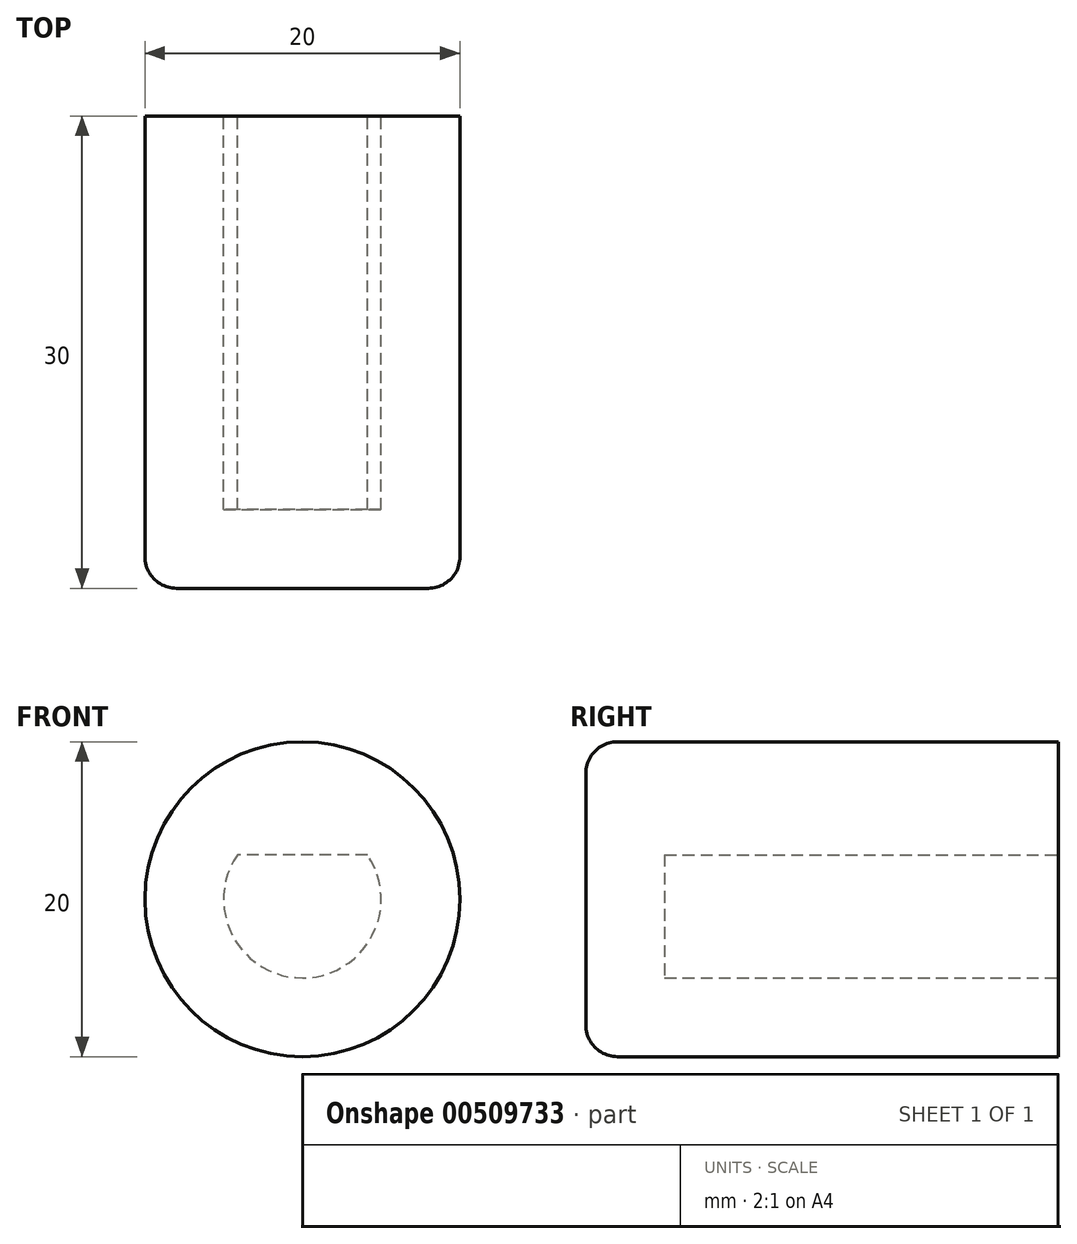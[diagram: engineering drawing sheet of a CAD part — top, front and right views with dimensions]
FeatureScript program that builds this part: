
annotation { "Feature Type Name" : "Feature", "Feature Type Description" : "" }
export const myFeature = defineFeature(function(context is Context, id is Id, definition is map)
    precondition{}
    {
        {
            var Q0;
            Q0=qCreatedBy(makeId("Front.planeOp"),FACE);
            cPlane(context, id + "F0", {"entities" : qUnion([Q0]), "cplaneType" : CPlaneType.OFFSET, "offset" : 30 * mm, "width" : 150 * mm, "height" : 150 * mm});
        }
        {
            var Q0;
            Q0=qCreatedBy(id+"F0.planeOp",FACE);
            var sketch = newSketch(context, id + "F1", { "sketchPlane" : qUnion([Q0])});
            skCircle(sketch, "E0", {"center": v(0, 0) * mm, "radius": 10 * mm});
            skSolve(sketch);
        }
        {
            var Q0;
            Q0=qCreatedBy(makeId("Front.planeOp"),FACE);
            var sketch = newSketch(context, id + "F2", { "sketchPlane" : qUnion([Q0])});
            skCircle(sketch, "E1", {"center": v(0, 0) * mm, "radius": 10 * mm});
            skSolve(sketch);
        }
        {
            var Q0;
            Q0=makeQuery(id+"F2.imprint","IMPRINT",FACE,{"disambiguationData":[TD([[makeQuery(id+"F2.imprint","IMPRINT",EDGE,{"derivedFrom":sQuery(id+"F2.wireOp",EDGE,"E1")}),1.0]])]});
            var Q1;
            Q1=makeQuery(id+"F1.imprint","IMPRINT",FACE,{"disambiguationData":[TD([[makeQuery(id+"F1.imprint","IMPRINT",EDGE,{"derivedFrom":sQuery(id+"F1.wireOp",EDGE,"E0")}),1.0]])]});
            loft(context, id + "F3", {"sheetProfilesArray" : [{ "sheetProfileEntities" : qUnion([Q0]) }, { "sheetProfileEntities" : qUnion([Q1]) }]});
        }
        {
            var Q0;
            Q0=makeQuery(id+"F3.opLoft","MID_CAP_EDGE",EDGE,{"disambiguationData":[OSD([sQuery(id+"F1.wireOp",EDGE,"E0"),sQuery(id+"F2.wireOp",EDGE,"E1")])],"capPos":1.0});
            fillet(context, id + "F4", {"entities" : qUnion([Q0]), "radius" : 2 * mm, "tangentPropagation" : true, "allowEdgeOverflow" : false});
        }
        {
            var Q0;
            Q0=qCreatedBy(makeId("Front.planeOp"),FACE);
            var sketch = newSketch(context, id + "F5", { "sketchPlane" : qUnion([Q0])});
            skCircle(sketch, "E2", {"center": v(0, 0) * mm, "radius": 5 * mm});
            skLineSegment(sketch, "E3", {"start": v(4.12, 2.83) * mm, "end": v(-4.12, 2.83) * mm});
            skSolve(sketch);
        }
        {
            var Q0;
            {var subQ0=sQuery(id+"F5.wireOp",EDGE,"E3");Q0=makeQuery(id+"F5.imprint","IMPRINT",FACE,{"disambiguationData":[TD([[makeQuery(id+"F5.imprint","IMPRINT",EDGE,{"derivedFrom":subQ0}),1.0]])]});}
            extrude(context, id + "F6", {"entities" : qUnion([Q0]), "operationType" : NewBodyOperationType.REMOVE, "depth" : 25 * mm, "offsetDistance" : 25 * mm});
        }
    });
